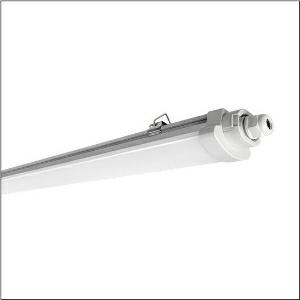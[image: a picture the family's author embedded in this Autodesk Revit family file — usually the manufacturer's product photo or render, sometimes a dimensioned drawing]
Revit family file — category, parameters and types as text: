
# Revit family: monsun_r__41_51fk20mn460a003_94ec
name_source: partatom
category: Lighting Fixtures
units: mm (PartAtom-declared; Revit-internal decimal feet)

## family parameters
Cut with Voids When Loaded = No
Host = Face
Light Source = No
Part Type = Normal
Room Calculation Point = No
Round Connector Dimension = Use Diameter
Shared = No

## types (1)
- --- (1 x LED, 6000 lm, 46 W, 4000K)
    Apparent Load = 46 VA
    CIE Flux Codes = 44 74 91 91 100
    Color Rendering = 80
    Color Temperature = 4000K
    Default Elevation = 1800 mm
    Description = Monsun® 41, damp-proof luminaire, primary optical cover: diffuser, of PC, frosted, light emission: direct distribution, primary light characteristic: symmetric, installation type: suspended mounting, surface-mounted, LED, rated luminous flux: 6.000lm, luminous efficacy: 130lm/W, light colour: 840, colour temperature: 4000K, control gear: ECG Multilumen, with terminal, 3-pole, through-wiring: 3x 1.5mm², mains connection: 220..240V, AC, 50/60Hz, rated input power: 46W, housing, luminaire housing, of PC, grey, length: 1.500mm, width: 79mm, height: 52mm, end cap, of PC, grey, ceiling mounting element, of stainless steel (V2A), protection rating (complete): IP65, insulation class (complete): insulation class II (safety insulation), certification: CE, UKCA, protection symbol: D, impact resistance: IK08, permissible operating ambient temperature: -20..+35°C, corresponds to IFS (International Featured Standards) requirements for safety and quality in the food industry, packaging unit: 1 piece
    Height = 54 mm
    Lamp = 1 x LED
    Lamp Light Flux = 6000 lm
    Lamp Power = 46 W
    Lamp count = 1
    Length = 1500 mm
    Luminous efficacy = 130 lm/W
    Manufacturer = Siteco
    ModVariant = No
    Model = 51FK20MN460A003
    Mounting Place = Ceiling
    Mounting Type = Surface mounted
    Number of Poles = 1
    OnlyDefault = Yes
    Power Factor = 1
    Product Name = Monsun® 41
    Product group = damp-proof luminaire | ceiling mounted
    ProductGroupID = 300
    Protection Class = Protection class II
    Protection Degree = IP 65
    RLX_Detail_Level = 1
    RlxData = <blob elided: 28741 chars, md5=bbe63cea>
    Socket = socket
    Standby Power = 0 W
    System Light Flux = 6000 lm
    System Power = 46 W
    Type Comments = factory setting: luminous flux: 100 % | (HIGH)
    Type Image = l_1007037.jpg
    URL = http://relux.com
    VarID = @adj_087095
    Voltage = 0 V
    Weight = 0.00 kg
    Width = 79 mm

## geometry (parser evidence)
native form markers: Blend x4, Sweep x13
no freeform markers — native parametric forms only
